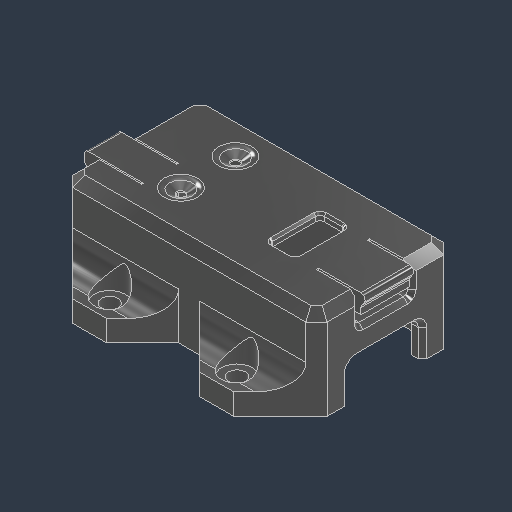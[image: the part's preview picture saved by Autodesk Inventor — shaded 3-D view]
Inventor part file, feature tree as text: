
AUTODESK INVENTOR PART (.ipt)
format: ipt  version: 2024.3 (Build 283343000, 343)  size: 3,077,632 bytes
history: native  units: in
note: dims shown in document units (in); Inventor stores cm internally (conversion verified against a paired STEP export)
features: other x19, sketch x13, extrude x11, fillet x8, chamfer x5, direct_edit x3, projected_geometry x3, hole x2, mirror x2, move_body x2, boolean_combine x1, thicken_offset x1, delete_face x1, revolve x1
ambient origin geometry x8: Origin, YZ Plane, XZ Plane, XY Plane, X Axis, Y Axis, Z Axis, Center Point
bodies: Solid19 (feature_tree), Solid1 (feature_tree), Solid2 (feature_tree), Solid3 (feature_tree), Solid4 (feature_tree), Solid5 (feature_tree), Solid6 (feature_tree), Solid7 (feature_tree), Solid8 (feature_tree), Solid10 (feature_tree), Solid11 (feature_tree), Solid12 (feature_tree), Solid14 (feature_tree), Solid15 (feature_tree), Solid16 (feature_tree), Solid17 (feature_tree), Solid18 (feature_tree)
feature tree (72):
  other  "CONTROLS,SPARK_MAX.ipt"
  boolean_combine  "Combine2"
  direct_edit  "Direct Edit1"
  direct_edit  "Direct Edit2"
  extrude  "Extrusion1"  TaperAngle=180.0deg  [1 undecoded]
  extrude  "Extrusion2"  Depth=1.625in
  thicken_offset  "Thicken1"
  fillet  "Fillet1"  Radius=3.0in
  fillet  "Fillet2"  Radius=1.0625in
  extrude  "Extrusion3"  Depth=0.01in
  extrude  "Extrusion4"  Depth=0.01in
  extrude  "Extrusion5"  Depth=0.5in TaperAngle=0.0deg
  sketch  "Sketch8"  dims[d25=0.018in d26=0.6in d27=0.0in]
  hole  "Hole1"  [1 undecoded]
  extrude  "Extrusion6"  Depth=0.6in TaperAngle=0.0deg
  extrude  "Extrusion7"  Depth=0.2749in
  extrude  "Extrusion8"  Depth=0.75in TaperAngle=0.0deg
  extrude  "Extrusion9"  Depth=0.1in
  extrude  "Extrusion10"  Depth=0.5in TaperAngle=0.0deg
  fillet  "Fillet6"  Radius=0.42in
  chamfer  "Chamfer3"  Distance=0.5in
  fillet  "Fillet7"  Radius=0.575in
  fillet  "Fillet8"  Radius=0.225in
  chamfer  "Chamfer4"  Distance=0.5in
  chamfer  "Chamfer5"  Distance=0.2405in
  chamfer  "Chamfer6"  Distance=0.06in
  chamfer  "Chamfer7"  Distance=0.05in
  fillet  "Fillet9"  Radius=0.75in
  extrude  "Extrusion11"  Depth=0.3125in
  hole  "Hole2"  [1 undecoded]
  fillet  "Fillet10"  Radius=0.05in
  mirror  "Mirror2"
  mirror  "Mirror3"
  fillet  "Fillet11"  Radius=0.05in
  delete_face  "Delete Face2"
  direct_edit  "Direct Edit3"
  other  "Solid1::CONTROLS,SPARK_MAX.ipt"
  other  "Solid2::CONTROLS,SPARK_MAX.ipt"
  other  "Solid3::CONTROLS,SPARK_MAX.ipt"
  other  "Solid4::CONTROLS,SPARK_MAX.ipt"
  other  "Solid5::CONTROLS,SPARK_MAX.ipt"
  other  "Solid6::CONTROLS,SPARK_MAX.ipt"
  other  "Solid7::CONTROLS,SPARK_MAX.ipt"
  other  "Solid8::CONTROLS,SPARK_MAX.ipt"
  other  "Solid9::CONTROLS,SPARK_MAX.ipt"
  other  "Solid10::CONTROLS,SPARK_MAX.ipt"
  other  "Solid11::CONTROLS,SPARK_MAX.ipt"
  other  "Solid12::CONTROLS,SPARK_MAX.ipt"
  other  "Solid14::CONTROLS,SPARK_MAX.ipt"
  other  "Solid15::CONTROLS,SPARK_MAX.ipt"
  other  "Solid16::CONTROLS,SPARK_MAX.ipt"
  other  "Solid17::CONTROLS,SPARK_MAX.ipt"
  other  "Solid18::CONTROLS,SPARK_MAX.ipt"
  other  "TaggingFeature1"
  sketch  "Sketch1"  dims[d0=0.3937in d1=180.0deg]
  sketch  "Sketch2"  dims[d2=0.0in d3=0.0in d4=0.1004in d5=1.625in d6=3.0in d7=1.0625in d8=0.0in]
  sketch  "Sketch3"  dims[d9=1.0in d10=0.0in d11=0.01in]
  sketch  "Sketch4"  dims[d12=0.01in d13=0.01in]
  sketch  "Sketch5"  dims[d14=0.025in d16=0.5in d17=0.0in]
  sketch  "Sketch6"  dims[d23=0.41in d24=0.34in]
  sketch  "Sketch9"  dims[d28=0.1in d29=0.2749in]
  sketch  "Sketch10"  dims[d30=0.125in d31=0.75in d32=0.0in]
  sketch  "Sketch11"  dims[d38=0.1in d39=0.75in d40=0.325in d41=0.25in d42=120.0deg d43=1.0in d44=0.8108in d46=0.1in]
  projected_geometry  "Projected Loop1"
  sketch  "Sketch12"  dims[d47=0.4in d48=0.5in d49=0.0in d50=0.42in]
  sketch  "Sketch13"  dims[d51=0.875in d52=0.5in d53=0.0in d54=0.575in d55=0.225in]
  projected_geometry  "Projected Loop2"
  projected_geometry  "Projected Loop3"
  sketch  "Sketch14"  dims[d56=0.025in d57=0.5in d58=0.0in d59=0.2405in d60=0.06in d61=0.05in d62=0.75in d63=0.0in d64=0.3125in d65=0.625in d66=0.0in d67=0.05in d68=0.05in d69=0.125in d70=45.0deg d71=0.34in d72=0.05in d73=0.1in d74=0.05in d75=0.125in d76=45.0deg d77=0.125in d78=0.125in d79=45.0deg d80=0.1in d81=0.125in d82=45.0deg d83=0.025in d84=0.125in d85=45.0deg d86=0.125in d88=0.4in d90=0.25in d91=0.0in d92=0.196in d93=0.75in d94=0.365in d95=0.0625in d96=120.0deg d97=1.0in d98=0.8108in d99=0.3in d103=2.05in d104=0.1875in d105=0.025in d106=0.01in d107=1.5in d108=0.0in d109=0.0in d110=0.31in d111=0.0in d112=0.0in d113=0.1731in]
  revolve  "Rotate1"  [1 undecoded]
  move_body  "Move1"
  move_body  "Move2"
note: 4 required parameter values undecoded (feature->parameter linkage not recoverable at this tier; creation-order binding heuristic only, values carry confidence <= 0.55)